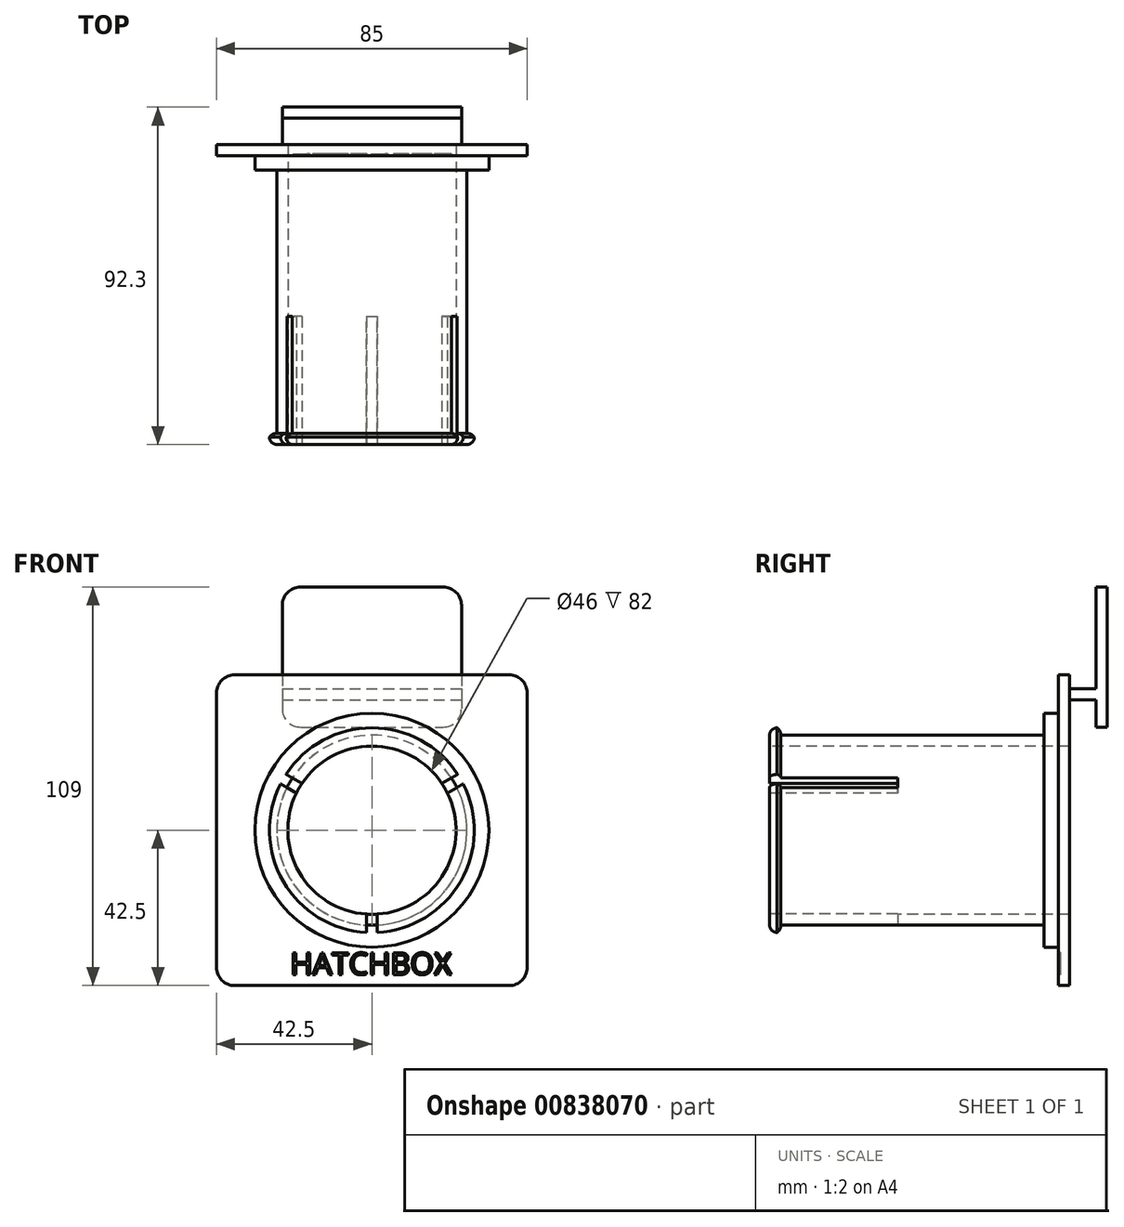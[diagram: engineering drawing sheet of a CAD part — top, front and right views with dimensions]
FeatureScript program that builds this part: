
annotation { "Feature Type Name" : "Feature", "Feature Type Description" : "" }
export const myFeature = defineFeature(function(context is Context, id is Id, definition is map)
    precondition{}
    {
        {
            assignVariable(context, id + "F0", {"name" : "BaseRingHeight", "anyValue" : 4});
        }
        {
            assignVariable(context, id + "F1", {"name" : "SpoolRingHeight", "anyValue" : 72});
        }
        {
            var Q0;
            Q0=qCreatedBy(makeId("Front.planeOp"),FACE);
            var sketch = newSketch(context, id + "F2", { "sketchPlane" : qUnion([Q0])});
            skLineSegment(sketch, "E0.bottom", {"start": v(-44, 38.3) * mm, "end": v(-5, 38.3) * mm});
            skLineSegment(sketch, "E0.top", {"start": v(-44, 0) * mm, "end": v(-5, 0) * mm});
            skLineSegment(sketch, "E0.left", {"start": v(-49, 33.3) * mm, "end": v(-49, 5) * mm});
            skLineSegment(sketch, "E0.right", {"start": v(0, 33.3) * mm, "end": v(0, 5) * mm});
            skPoint(sketch, "E1.visualSharp", {"position": v(-49, 38.3) * mm});
            skArc(sketch, "E1.filletArc", {"start": v(-44, 38.3) * mm, "mid": v(-47.54, 36.84) * mm, "end": v(-49, 33.3) * mm});
            skPoint(sketch, "E2.visualSharp", {"position": v(0, 38.3) * mm});
            skArc(sketch, "E2.filletArc", {"start": v(0, 33.3) * mm, "mid": v(-1.46, 36.84) * mm, "end": v(-5, 38.3) * mm});
            skPoint(sketch, "E3.visualSharp", {"position": v(0, 0) * mm});
            skArc(sketch, "E3.filletArc", {"start": v(-5, 0) * mm, "mid": v(-1.46, 1.46) * mm, "end": v(0, 5) * mm});
            skPoint(sketch, "E4.visualSharp", {"position": v(-49, 0) * mm});
            skArc(sketch, "E4.filletArc", {"start": v(-49, 5) * mm, "mid": v(-47.54, 1.46) * mm, "end": v(-44, 0) * mm});
            skSolve(sketch);
        }
        {
            var Q0;
            Q0=qSketchRegion(id+"F2",true);
            extrude(context, id + "F3", {"entities" : qUnion([Q0]), "depth" : 3 * mm, "offsetDistance" : 25 * mm});
        }
        {
            var Q0;
            Q0=makeQuery(id+"F3.opExtrude","CAP_FACE",FACE,{"disambiguationData":[OSD([sQuery(id+"F2.wireOp",EDGE,"E0.bottom"),sQuery(id+"F2.wireOp",EDGE,"E0.top"),sQuery(id+"F2.wireOp",EDGE,"E0.left"),sQuery(id+"F2.wireOp",EDGE,"E0.right")])],"isStart":false});
            var sketch = newSketch(context, id + "F4", { "sketchPlane" : qUnion([Q0])});
            skLineSegment(sketch, "E5.bottom", {"start": v(-49, 10.5) * mm, "end": v(0, 10.5) * mm});
            skLineSegment(sketch, "E5.top", {"start": v(-49, 7.5) * mm, "end": v(0, 7.5) * mm});
            skLineSegment(sketch, "E5.left", {"start": v(-49, 10.5) * mm, "end": v(-49, 7.5) * mm});
            skLineSegment(sketch, "E5.right", {"start": v(0, 10.5) * mm, "end": v(0, 7.5) * mm});
            skSolve(sketch);
        }
        {
            var Q0;
            Q0=qSketchRegion(id+"F4",true);
            extrude(context, id + "F5", {"entities" : qUnion([Q0]), "operationType" : NewBodyOperationType.ADD, "depth" : 7.3 * mm, "offsetDistance" : 25 * mm});
        }
        {
            var Q0;
            Q0=makeQuery(id+"F5.opExtrude","CAP_FACE",FACE,{"disambiguationData":[OSD([sQuery(id+"F4.wireOp",EDGE,"E5.bottom"),sQuery(id+"F4.wireOp",EDGE,"E5.top"),sQuery(id+"F4.wireOp",EDGE,"E5.left"),sQuery(id+"F4.wireOp",EDGE,"E5.right")])],"isStart":false});
            var sketch = newSketch(context, id + "F6", { "sketchPlane" : qUnion([Q0])});
            skLineSegment(sketch, "E6.bottom", {"start": v(-62, 14.3) * mm, "end": v(13, 14.3) * mm});
            skLineSegment(sketch, "E6.top", {"start": v(-62, -70.7) * mm, "end": v(13, -70.7) * mm});
            skLineSegment(sketch, "E6.left", {"start": v(-67, 9.3) * mm, "end": v(-67, -65.7) * mm});
            skLineSegment(sketch, "E6.right", {"start": v(18, 9.3) * mm, "end": v(18, -65.7) * mm});
            skPoint(sketch, "E7.visualSharp", {"position": v(-67, 14.3) * mm});
            skArc(sketch, "E7.filletArc", {"start": v(-62, 14.3) * mm, "mid": v(-65.54, 12.84) * mm, "end": v(-67, 9.3) * mm});
            skPoint(sketch, "E8.visualSharp", {"position": v(18, 14.3) * mm});
            skArc(sketch, "E8.filletArc", {"start": v(18, 9.3) * mm, "mid": v(16.54, 12.84) * mm, "end": v(13, 14.3) * mm});
            skPoint(sketch, "E9.visualSharp", {"position": v(18, -70.7) * mm});
            skArc(sketch, "E9.filletArc", {"start": v(13, -70.7) * mm, "mid": v(16.54, -69.24) * mm, "end": v(18, -65.7) * mm});
            skPoint(sketch, "E10.visualSharp", {"position": v(-67, -70.7) * mm});
            skArc(sketch, "E10.filletArc", {"start": v(-67, -65.7) * mm, "mid": v(-65.54, -69.24) * mm, "end": v(-62, -70.7) * mm});
            skSolve(sketch);
        }
        {
            var Q0;
            Q0=qSketchRegion(id+"F6",true);
            extrude(context, id + "F7", {"entities" : qUnion([Q0]), "operationType" : NewBodyOperationType.ADD, "depth" : 3 * mm, "offsetDistance" : 25 * mm});
        }
        {
            var Q0;
            Q0=makeQuery(id+"F7.opExtrude","CAP_FACE",FACE,{"disambiguationData":[OSD([sQuery(id+"F6.wireOp",EDGE,"E6.bottom"),sQuery(id+"F6.wireOp",EDGE,"E6.top"),sQuery(id+"F6.wireOp",EDGE,"E6.left"),sQuery(id+"F6.wireOp",EDGE,"E6.right"),sQuery(id+"F6.wireOp",EDGE,"E7.filletArc"),sQuery(id+"F6.wireOp",EDGE,"E8.filletArc"),sQuery(id+"F6.wireOp",EDGE,"E9.filletArc"),sQuery(id+"F6.wireOp",EDGE,"E10.filletArc")])],"isStart":false});
            var sketch = newSketch(context, id + "F8", { "sketchPlane" : qUnion([Q0])});
            skCircle(sketch, "E11", {"center": v(-24.5, -28.2) * mm, "radius": 32 * mm});
            skLineSegment(sketch, "E12", {"start": v(-82.43, -28.2) * mm, "end": v(118.43, -28.2) * mm, "construction": true});
            skLineSegment(sketch, "E13", {"start": v(-24.5, 43.68) * mm, "end": v(-24.5, -185.08) * mm, "construction": true});
            skSolve(sketch);
        }
        {
            var Q0;
            Q0=qSketchRegion(id+"F8",true);
            extrude(context, id + "F9", {"entities" : qUnion([Q0]), "operationType" : NewBodyOperationType.ADD, "depth" : (getVariable(context, 'BaseRingHeight')) * mm, "offsetDistance" : 25 * mm});
        }
        {
            var Q0;
            Q0=makeQuery(id+"F9.opExtrude","CAP_FACE",FACE,{"disambiguationData":[OSD([sQuery(id+"F8.wireOp",EDGE,"E11")])],"isStart":false});
            var sketch = newSketch(context, id + "F10", { "sketchPlane" : qUnion([Q0])});
            skCircle(sketch, "E14", {"center": v(-24.5, -28.2) * mm, "radius": 26 * mm});
            skSolve(sketch);
        }
        {
            var Q0;
            Q0=qSketchRegion(id+"F10",true);
            var Q1;
            Q1=qSketchRegion(id+"F12",true);
            extrude(context, id + "F11", {"entities" : qUnion([Q0, Q1]), "operationType" : NewBodyOperationType.ADD, "depth" : (getVariable(context, 'SpoolRingHeight')) * mm, "offsetDistance" : 25 * mm});
        }
        {
            var Q0;
            Q0=makeQuery(id+"F11.opExtrude","CAP_FACE",FACE,{"disambiguationData":[OSD([sQuery(id+"F10.wireOp",EDGE,"E14")])],"isStart":false});
            var sketch = newSketch(context, id + "F12", { "sketchPlane" : qUnion([Q0])});
            skCircle(sketch, "E15", {"center": v(-24.5, -28.2) * mm, "radius": 23 * mm});
            skSolve(sketch);
        }
        {
            var Q0;
            Q0=qSketchRegion(id+"F12",true);
            var Q1;
            Q1=makeQuery(id+"F7.opExtrude","CAP_FACE",FACE,{"disambiguationData":[OSD([sQuery(id+"F6.wireOp",EDGE,"E6.bottom"),sQuery(id+"F6.wireOp",EDGE,"E6.top"),sQuery(id+"F6.wireOp",EDGE,"E6.left"),sQuery(id+"F6.wireOp",EDGE,"E6.right"),sQuery(id+"F6.wireOp",EDGE,"E7.filletArc"),sQuery(id+"F6.wireOp",EDGE,"E8.filletArc"),sQuery(id+"F6.wireOp",EDGE,"E9.filletArc"),sQuery(id+"F6.wireOp",EDGE,"E10.filletArc")])],"isStart":true});
            extrude(context, id + "F13", {"entities" : qUnion([Q0]), "operationType" : NewBodyOperationType.REMOVE, "endBound" : BoundingType.UP_TO_SURFACE, "oppositeDirection" : true, "depth" : 25 * mm, "endBoundEntityFace" : qUnion([Q1]), "offsetDistance" : 25 * mm});
        }
        {
            var Q0;
            {var subQ0=sQuery(id+"F10.wireOp",EDGE,"E14");Q0=makeQuery(id+"F17.boolean.opBoolean","SPLIT",FACE,{"disambiguationData":[TD([makeQuery(id+"F17.opExtrude","SWEPT_FACE",FACE,{"disambiguationData":[OSD([sQuery(id+"F16.wireOp",EDGE,"E21.left")])]})])],"derivedFrom":makeQuery(id+"F11.opExtrude","CAP_FACE",FACE,{"disambiguationData":[OSD([subQ0])],"isStart":false})});}
            var sketch = newSketch(context, id + "F14", { "sketchPlane" : qUnion([Q0])});
            skCircle(sketch, "E16", {"center": v(-24.5, -28.2) * mm, "radius": 23 * mm});
            skCircle(sketch, "E17", {"center": v(-24.5, -28.2) * mm, "radius": 28 * mm});
            skSolve(sketch);
        }
        {
            var Q0;
            Q0=qSketchRegion(id+"F14",true);
            extrude(context, id + "F15", {"entities" : qUnion([Q0]), "operationType" : NewBodyOperationType.ADD, "depth" : 3 * mm, "offsetDistance" : 25 * mm});
        }
        {
            var Q0;
            Q0=makeQuery(id+"F15.opExtrude","CAP_FACE",FACE,{"disambiguationData":[OSD([sQuery(id+"F14.wireOp",EDGE,"E16"),sQuery(id+"F14.wireOp",EDGE,"E17")])],"isStart":false});
            var sketch = newSketch(context, id + "F16", { "sketchPlane" : qUnion([Q0])});
            skLineSegment(sketch, "E18", {"start": v(-24.5, -28.2) * mm, "end": v(-51, -12.9) * mm, "construction": true});
            skLineSegment(sketch, "E19", {"start": v(-24.5, -28.2) * mm, "end": v(2, -12.9) * mm, "construction": true});
            skLineSegment(sketch, "E20", {"start": v(-24.5, -28.2) * mm, "end": v(-24.5, -58.8) * mm, "construction": true});
            skLineSegment(sketch, "E21.bottom", {"start": v(-26, -28.2) * mm, "end": v(-23, -28.2) * mm});
            skLineSegment(sketch, "E21.top", {"start": v(-26, -58.76) * mm, "end": v(-23, -58.76) * mm});
            skLineSegment(sketch, "E21.left", {"start": v(-26, -28.2) * mm, "end": v(-26, -58.76) * mm});
            skLineSegment(sketch, "E21.right", {"start": v(-23, -28.2) * mm, "end": v(-23, -58.76) * mm});
            skCircle(sketch, "E22", {"center": v(-24.5, -28.2) * mm, "radius": 30.6 * mm, "construction": true});
            skLineSegment(sketch, "E23", {"start": v(1.22, -11.62) * mm, "end": v(2.72, -14.22) * mm});
            skLineSegment(sketch, "E24", {"start": v(2.72, -14.22) * mm, "end": v(-23.75, -29.5) * mm});
            skLineSegment(sketch, "E25", {"start": v(-23.75, -29.5) * mm, "end": v(-25.25, -26.9) * mm});
            skLineSegment(sketch, "E26", {"start": v(-25.25, -26.9) * mm, "end": v(1.22, -11.62) * mm});
            skLineSegment(sketch, "E27", {"start": v(-50.22, -11.62) * mm, "end": v(-51.72, -14.22) * mm});
            skLineSegment(sketch, "E28", {"start": v(-51.72, -14.22) * mm, "end": v(-25.25, -29.5) * mm});
            skLineSegment(sketch, "E29", {"start": v(-25.25, -29.5) * mm, "end": v(-23.75, -26.9) * mm});
            skLineSegment(sketch, "E30", {"start": v(-23.75, -26.9) * mm, "end": v(-50.22, -11.62) * mm});
            skSolve(sketch);
        }
        {
            var Q0;
            Q0=qSketchRegion(id+"F16",true);
            extrude(context, id + "F17", {"entities" : qUnion([Q0]), "operationType" : NewBodyOperationType.REMOVE, "oppositeDirection" : true, "depth" : 70 * mm, "offsetDistance" : 25 * mm, "symmetric" : true});
        }
        {
            var Q0;
            {var subQ0=sQuery(id+"F14.wireOp",EDGE,"E17");Q0=makeQuery(id+"F17.boolean.opBoolean","SPLIT",EDGE,{"disambiguationData":[TD([makeQuery(id+"F17.opExtrude","SWEPT_FACE",FACE,{"disambiguationData":[OSD([sQuery(id+"F16.wireOp",EDGE,"E21.left")])]})])],"derivedFrom":makeQuery(id+"F15.opExtrude","CAP_EDGE",EDGE,{"disambiguationData":[OSD([subQ0])],"isStart":false})});}
            var Q1;
            {var subQ0=sQuery(id+"F14.wireOp",EDGE,"E17");Q1=makeQuery(id+"F17.boolean.opBoolean","SPLIT",EDGE,{"disambiguationData":[TD([makeQuery(id+"F17.opExtrude","SWEPT_FACE",FACE,{"disambiguationData":[OSD([sQuery(id+"F16.wireOp",EDGE,"E26")])]})])],"derivedFrom":makeQuery(id+"F15.opExtrude","CAP_EDGE",EDGE,{"disambiguationData":[OSD([subQ0])],"isStart":false})});}
            var Q2;
            {var subQ0=sQuery(id+"F14.wireOp",EDGE,"E17");Q2=makeQuery(id+"F17.boolean.opBoolean","SPLIT",EDGE,{"disambiguationData":[TD([makeQuery(id+"F17.opExtrude","SWEPT_FACE",FACE,{"disambiguationData":[OSD([sQuery(id+"F16.wireOp",EDGE,"E21.right")])]})])],"derivedFrom":makeQuery(id+"F15.opExtrude","CAP_EDGE",EDGE,{"disambiguationData":[OSD([subQ0])],"isStart":false})});}
            fillet(context, id + "F18", {"entities" : qUnion([Q0, Q1, Q2]), "radius" : 2 * mm, "tangentPropagation" : true, "allowEdgeOverflow" : false});
        }
        {
            var Q0;
            {var subQ0=sQuery(id+"F14.wireOp",EDGE,"E17");Q0=makeQuery(id+"F17.boolean.opBoolean","SPLIT",EDGE,{"disambiguationData":[TD([makeQuery(id+"F17.opExtrude","SWEPT_FACE",FACE,{"disambiguationData":[OSD([sQuery(id+"F16.wireOp",EDGE,"E21.right")])]})])],"derivedFrom":makeQuery(id+"F15.opExtrude","CAP_EDGE",EDGE,{"disambiguationData":[OSD([subQ0])],"isStart":true})});}
            var Q1;
            {var subQ0=sQuery(id+"F14.wireOp",EDGE,"E17");Q1=makeQuery(id+"F17.boolean.opBoolean","SPLIT",EDGE,{"disambiguationData":[TD([makeQuery(id+"F17.opExtrude","SWEPT_FACE",FACE,{"disambiguationData":[OSD([sQuery(id+"F16.wireOp",EDGE,"E26")])]})])],"derivedFrom":makeQuery(id+"F15.opExtrude","CAP_EDGE",EDGE,{"disambiguationData":[OSD([subQ0])],"isStart":true})});}
            var Q2;
            {var subQ0=sQuery(id+"F14.wireOp",EDGE,"E17");Q2=makeQuery(id+"F17.boolean.opBoolean","SPLIT",EDGE,{"disambiguationData":[TD([makeQuery(id+"F17.opExtrude","SWEPT_FACE",FACE,{"disambiguationData":[OSD([sQuery(id+"F16.wireOp",EDGE,"E21.left")])]})])],"derivedFrom":makeQuery(id+"F15.opExtrude","CAP_EDGE",EDGE,{"disambiguationData":[OSD([subQ0])],"isStart":true})});}
            fillet(context, id + "F19", {"entities" : qUnion([Q0, Q1, Q2]), "radius" : 2 * mm, "tangentPropagation" : true, "allowEdgeOverflow" : false});
        }
        {
            var Q0;
            Q0=makeQuery(id+"F7.opExtrude","CAP_FACE",FACE,{"disambiguationData":[OSD([sQuery(id+"F6.wireOp",EDGE,"E6.bottom"),sQuery(id+"F6.wireOp",EDGE,"E6.top"),sQuery(id+"F6.wireOp",EDGE,"E6.left"),sQuery(id+"F6.wireOp",EDGE,"E6.right"),sQuery(id+"F6.wireOp",EDGE,"E7.filletArc"),sQuery(id+"F6.wireOp",EDGE,"E8.filletArc"),sQuery(id+"F6.wireOp",EDGE,"E9.filletArc"),sQuery(id+"F6.wireOp",EDGE,"E10.filletArc")])],"isStart":false});
            var sketch = newSketch(context, id + "F20", { "sketchPlane" : qUnion([Q0])});
            skText(sketch, "E31", { "text": "HATCHBOX", "fontName": "OpenSans-Regular.ttf"});
            skLineSegment(sketch, "E32", {"start": v(14.01, -67.7) * mm, "end": v(-56.31, -67.7) * mm, "construction": true});
            const initialGuessF20  = {"E31": [-0.04682, -0.0677, 1, 0, 0.006]};
            skSetInitialGuess(sketch, initialGuessF20);
            skSolve(sketch);
        }
        {
            var Q0;
            Q0=qSketchRegion(id+"F20",true);
            extrude(context, id + "F21", {"entities" : qUnion([Q0]), "operationType" : NewBodyOperationType.REMOVE, "oppositeDirection" : true, "depth" : .5 * mm, "offsetDistance" : 25 * mm});
        }
    });
